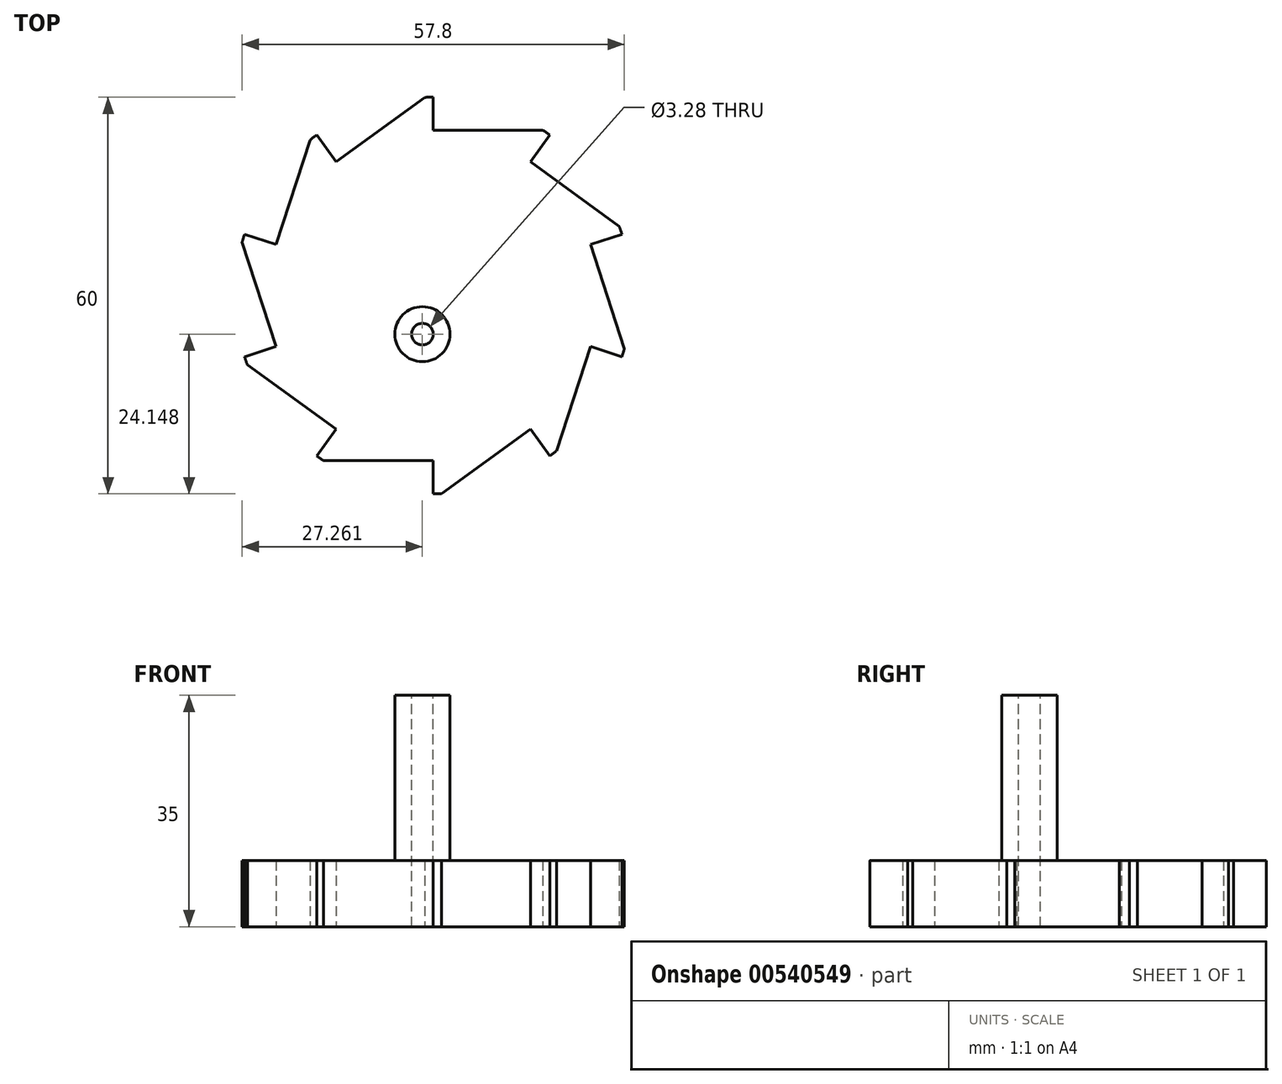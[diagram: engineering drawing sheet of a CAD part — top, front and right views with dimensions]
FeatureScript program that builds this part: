
annotation { "Feature Type Name" : "Feature", "Feature Type Description" : "" }
export const myFeature = defineFeature(function(context is Context, id is Id, definition is map)
    precondition{}
    {
        {
            var Q0;
            Q0=qCreatedBy(makeId("Top.planeOp"),FACE);
            var sketch = newSketch(context, id + "F0", { "sketchPlane" : qUnion([Q0])});
            skArc(sketch, "E0", {"start": v(0, 30) * mm, "mid": v(-0.64, 30) * mm, "end": v(-1.28, 29.97) * mm});
            skLineSegment(sketch, "E1", {"start": v(0, 30) * mm, "end": v(0, 25) * mm});
            skLineSegment(sketch, "E2", {"start": v(0, 25) * mm, "end": v(16.58, 25) * mm});
            skLineSegment(sketch, "E3.1.0", {"start": v(-17.63, 24.27) * mm, "end": v(-14.7, 20.23) * mm});
            skLineSegment(sketch, "E3.1.1", {"start": v(-14.7, 20.23) * mm, "end": v(-1.28, 29.97) * mm});
            skLineSegment(sketch, "E3.2.0", {"start": v(-28.53, 9.27) * mm, "end": v(-23.78, 7.73) * mm});
            skLineSegment(sketch, "E3.2.1", {"start": v(-23.78, 7.73) * mm, "end": v(-18.65, 23.5) * mm});
            skLineSegment(sketch, "E3.3.0", {"start": v(-28.53, -9.27) * mm, "end": v(-23.78, -7.73) * mm});
            skLineSegment(sketch, "E3.3.1", {"start": v(-23.78, -7.73) * mm, "end": v(-28.9, 8.05) * mm});
            skLineSegment(sketch, "E3.4.0", {"start": v(-17.63, -24.27) * mm, "end": v(-14.7, -20.23) * mm});
            skLineSegment(sketch, "E3.4.1", {"start": v(-14.7, -20.23) * mm, "end": v(-28.11, -10.48) * mm});
            skLineSegment(sketch, "E3.5.0", {"start": v(0, -30) * mm, "end": v(0, -25) * mm});
            skLineSegment(sketch, "E3.5.1", {"start": v(0, -25) * mm, "end": v(-16.58, -25) * mm});
            skLineSegment(sketch, "E3.6.0", {"start": v(17.63, -24.27) * mm, "end": v(14.7, -20.23) * mm});
            skLineSegment(sketch, "E3.6.1", {"start": v(14.7, -20.23) * mm, "end": v(1.28, -29.97) * mm});
            skLineSegment(sketch, "E3.7.0", {"start": v(28.53, -9.27) * mm, "end": v(23.78, -7.73) * mm});
            skLineSegment(sketch, "E3.7.1", {"start": v(23.78, -7.73) * mm, "end": v(18.65, -23.5) * mm});
            skLineSegment(sketch, "E3.8.0", {"start": v(28.53, 9.27) * mm, "end": v(23.78, 7.73) * mm});
            skLineSegment(sketch, "E3.8.1", {"start": v(23.78, 7.73) * mm, "end": v(28.9, -8.05) * mm});
            skLineSegment(sketch, "E3.9.0", {"start": v(17.63, 24.27) * mm, "end": v(14.7, 20.23) * mm});
            skLineSegment(sketch, "E3.9.1", {"start": v(14.7, 20.23) * mm, "end": v(28.11, 10.48) * mm});
            skArc(sketch, "E4.trimOffspring", {"start": v(17.63, 24.27) * mm, "mid": v(17.11, 24.64) * mm, "end": v(16.58, 25) * mm});
            skArc(sketch, "E5.trimOffspring", {"start": v(28.53, 9.27) * mm, "mid": v(28.33, 9.88) * mm, "end": v(28.11, 10.48) * mm});
            skArc(sketch, "E6.trimOffspring", {"start": v(28.53, -9.27) * mm, "mid": v(28.72, -8.66) * mm, "end": v(28.9, -8.05) * mm});
            skArc(sketch, "E7.trimOffspring", {"start": v(17.63, -24.27) * mm, "mid": v(18.15, -23.89) * mm, "end": v(18.65, -23.5) * mm});
            skArc(sketch, "E8.trimOffspring", {"start": v(0, -30) * mm, "mid": v(0.64, -30) * mm, "end": v(1.28, -29.97) * mm});
            skArc(sketch, "E9.trimOffspring", {"start": v(-17.63, -24.27) * mm, "mid": v(-17.11, -24.64) * mm, "end": v(-16.58, -25) * mm});
            skArc(sketch, "E10.trimOffspring", {"start": v(-28.53, -9.27) * mm, "mid": v(-28.33, -9.88) * mm, "end": v(-28.11, -10.48) * mm});
            skArc(sketch, "E11.trimOffspring", {"start": v(-28.53, 9.27) * mm, "mid": v(-28.72, 8.66) * mm, "end": v(-28.9, 8.05) * mm});
            skArc(sketch, "E12.trimOffspring", {"start": v(-17.63, 24.27) * mm, "mid": v(-18.15, 23.89) * mm, "end": v(-18.65, 23.5) * mm});
            skSolve(sketch);
        }
        {
            var Q0;
            Q0 = qSketchRegion(id + "F0", true);
            extrude(context, id + "F1", {"entities" : qUnion([Q0]), "depth" : 10 * mm, "offsetDistance" : 25 * mm});
        }
        {
            var Q0;
            Q0=makeQuery(id+"F1.opExtrude","CAP_FACE",FACE,{"disambiguationData":[OSD([sQuery(id+"F0.wireOp",EDGE,"E0"),sQuery(id+"F0.wireOp",EDGE,"E1"),sQuery(id+"F0.wireOp",EDGE,"E2"),sQuery(id+"F0.wireOp",EDGE,"E3.1.0"),sQuery(id+"F0.wireOp",EDGE,"E3.1.1"),sQuery(id+"F0.wireOp",EDGE,"E3.2.0"),sQuery(id+"F0.wireOp",EDGE,"E3.2.1"),sQuery(id+"F0.wireOp",EDGE,"E3.3.0"),sQuery(id+"F0.wireOp",EDGE,"E3.3.1"),sQuery(id+"F0.wireOp",EDGE,"E3.4.0"),sQuery(id+"F0.wireOp",EDGE,"E3.4.1"),sQuery(id+"F0.wireOp",EDGE,"E3.5.0"),sQuery(id+"F0.wireOp",EDGE,"E3.5.1"),sQuery(id+"F0.wireOp",EDGE,"E3.6.0"),sQuery(id+"F0.wireOp",EDGE,"E3.6.1"),sQuery(id+"F0.wireOp",EDGE,"E3.7.0"),sQuery(id+"F0.wireOp",EDGE,"E3.7.1"),sQuery(id+"F0.wireOp",EDGE,"E3.8.0"),sQuery(id+"F0.wireOp",EDGE,"E3.8.1"),sQuery(id+"F0.wireOp",EDGE,"E3.9.0"),sQuery(id+"F0.wireOp",EDGE,"E3.9.1"),sQuery(id+"F0.wireOp",EDGE,"E4.trimOffspring"),sQuery(id+"F0.wireOp",EDGE,"E5.trimOffspring"),sQuery(id+"F0.wireOp",EDGE,"E6.trimOffspring"),sQuery(id+"F0.wireOp",EDGE,"E7.trimOffspring"),sQuery(id+"F0.wireOp",EDGE,"E8.trimOffspring"),sQuery(id+"F0.wireOp",EDGE,"E9.trimOffspring"),sQuery(id+"F0.wireOp",EDGE,"E10.trimOffspring"),sQuery(id+"F0.wireOp",EDGE,"E11.trimOffspring"),sQuery(id+"F0.wireOp",EDGE,"E12.trimOffspring")])],"isStart":false});
            var sketch = newSketch(context, id + "F2", { "sketchPlane" : qUnion([Q0])});
            skCircle(sketch, "E13", {"center": v(-1.64, -5.85) * mm, "radius": 4.17 * mm});
            skSolve(sketch);
        }
        {
            var Q0;
            Q0=makeQuery(id+"F2.imprint","IMPRINT",FACE,{"disambiguationData":[TD([[makeQuery(id+"F2.imprint","IMPRINT",EDGE,{"derivedFrom":sQuery(id+"F2.wireOp",EDGE,"E13")}),1.0]])]});
            extrude(context, id + "F3", {"entities" : qUnion([Q0]), "operationType" : NewBodyOperationType.ADD, "depth" : 25 * mm, "offsetDistance" : 25 * mm});
        }
        {
            var Q0;
            Q0=makeQuery(id+"F1.opExtrude","CAP_FACE",FACE,{"disambiguationData":[OSD([sQuery(id+"F0.wireOp",EDGE,"E0"),sQuery(id+"F0.wireOp",EDGE,"E1"),sQuery(id+"F0.wireOp",EDGE,"E2"),sQuery(id+"F0.wireOp",EDGE,"E3.1.0"),sQuery(id+"F0.wireOp",EDGE,"E3.1.1"),sQuery(id+"F0.wireOp",EDGE,"E3.2.0"),sQuery(id+"F0.wireOp",EDGE,"E3.2.1"),sQuery(id+"F0.wireOp",EDGE,"E3.3.0"),sQuery(id+"F0.wireOp",EDGE,"E3.3.1"),sQuery(id+"F0.wireOp",EDGE,"E3.4.0"),sQuery(id+"F0.wireOp",EDGE,"E3.4.1"),sQuery(id+"F0.wireOp",EDGE,"E3.5.0"),sQuery(id+"F0.wireOp",EDGE,"E3.5.1"),sQuery(id+"F0.wireOp",EDGE,"E3.6.0"),sQuery(id+"F0.wireOp",EDGE,"E3.6.1"),sQuery(id+"F0.wireOp",EDGE,"E3.7.0"),sQuery(id+"F0.wireOp",EDGE,"E3.7.1"),sQuery(id+"F0.wireOp",EDGE,"E3.8.0"),sQuery(id+"F0.wireOp",EDGE,"E3.8.1"),sQuery(id+"F0.wireOp",EDGE,"E3.9.0"),sQuery(id+"F0.wireOp",EDGE,"E3.9.1"),sQuery(id+"F0.wireOp",EDGE,"E4.trimOffspring"),sQuery(id+"F0.wireOp",EDGE,"E5.trimOffspring"),sQuery(id+"F0.wireOp",EDGE,"E6.trimOffspring"),sQuery(id+"F0.wireOp",EDGE,"E7.trimOffspring"),sQuery(id+"F0.wireOp",EDGE,"E8.trimOffspring"),sQuery(id+"F0.wireOp",EDGE,"E9.trimOffspring"),sQuery(id+"F0.wireOp",EDGE,"E10.trimOffspring"),sQuery(id+"F0.wireOp",EDGE,"E11.trimOffspring"),sQuery(id+"F0.wireOp",EDGE,"E12.trimOffspring")])],"isStart":false});
            var sketch = newSketch(context, id + "F4", { "sketchPlane" : qUnion([Q0])});
            skCircle(sketch, "E14", {"center": v(-1.64, -5.85) * mm, "radius": 1.64 * mm});
            skSolve(sketch);
        }
        {
            var Q0;
            Q0 = qSketchRegion(id + "F4", true);
            extrude(context, id + "F5", {"entities" : qUnion([Q0]), "operationType" : NewBodyOperationType.REMOVE, "oppositeDirection" : true, "depth" : 25 * mm, "offsetDistance" : 25 * mm});
        }
        {
            var Q0;
            Q0=makeQuery(id+"F1.opExtrude","CAP_FACE",FACE,{"disambiguationData":[OSD([sQuery(id+"F0.wireOp",EDGE,"E0"),sQuery(id+"F0.wireOp",EDGE,"E1"),sQuery(id+"F0.wireOp",EDGE,"E2"),sQuery(id+"F0.wireOp",EDGE,"E3.1.0"),sQuery(id+"F0.wireOp",EDGE,"E3.1.1"),sQuery(id+"F0.wireOp",EDGE,"E3.2.0"),sQuery(id+"F0.wireOp",EDGE,"E3.2.1"),sQuery(id+"F0.wireOp",EDGE,"E3.3.0"),sQuery(id+"F0.wireOp",EDGE,"E3.3.1"),sQuery(id+"F0.wireOp",EDGE,"E3.4.0"),sQuery(id+"F0.wireOp",EDGE,"E3.4.1"),sQuery(id+"F0.wireOp",EDGE,"E3.5.0"),sQuery(id+"F0.wireOp",EDGE,"E3.5.1"),sQuery(id+"F0.wireOp",EDGE,"E3.6.0"),sQuery(id+"F0.wireOp",EDGE,"E3.6.1"),sQuery(id+"F0.wireOp",EDGE,"E3.7.0"),sQuery(id+"F0.wireOp",EDGE,"E3.7.1"),sQuery(id+"F0.wireOp",EDGE,"E3.8.0"),sQuery(id+"F0.wireOp",EDGE,"E3.8.1"),sQuery(id+"F0.wireOp",EDGE,"E3.9.0"),sQuery(id+"F0.wireOp",EDGE,"E3.9.1"),sQuery(id+"F0.wireOp",EDGE,"E4.trimOffspring"),sQuery(id+"F0.wireOp",EDGE,"E5.trimOffspring"),sQuery(id+"F0.wireOp",EDGE,"E6.trimOffspring"),sQuery(id+"F0.wireOp",EDGE,"E7.trimOffspring"),sQuery(id+"F0.wireOp",EDGE,"E8.trimOffspring"),sQuery(id+"F0.wireOp",EDGE,"E9.trimOffspring"),sQuery(id+"F0.wireOp",EDGE,"E10.trimOffspring"),sQuery(id+"F0.wireOp",EDGE,"E11.trimOffspring"),sQuery(id+"F0.wireOp",EDGE,"E12.trimOffspring")])],"isStart":false});
            var sketch = newSketch(context, id + "F6", { "sketchPlane" : qUnion([Q0])});
            skCircle(sketch, "E15", {"center": v(-1.64, -5.85) * mm, "radius": 1.64 * mm});
            skSolve(sketch);
        }
        {
            var Q0;
            Q0 = qSketchRegion(id + "F6", true);
            extrude(context, id + "F7", {"entities" : qUnion([Q0]), "operationType" : NewBodyOperationType.REMOVE, "depth" : 47.6 * mm, "offsetDistance" : 25 * mm});
        }
    });
